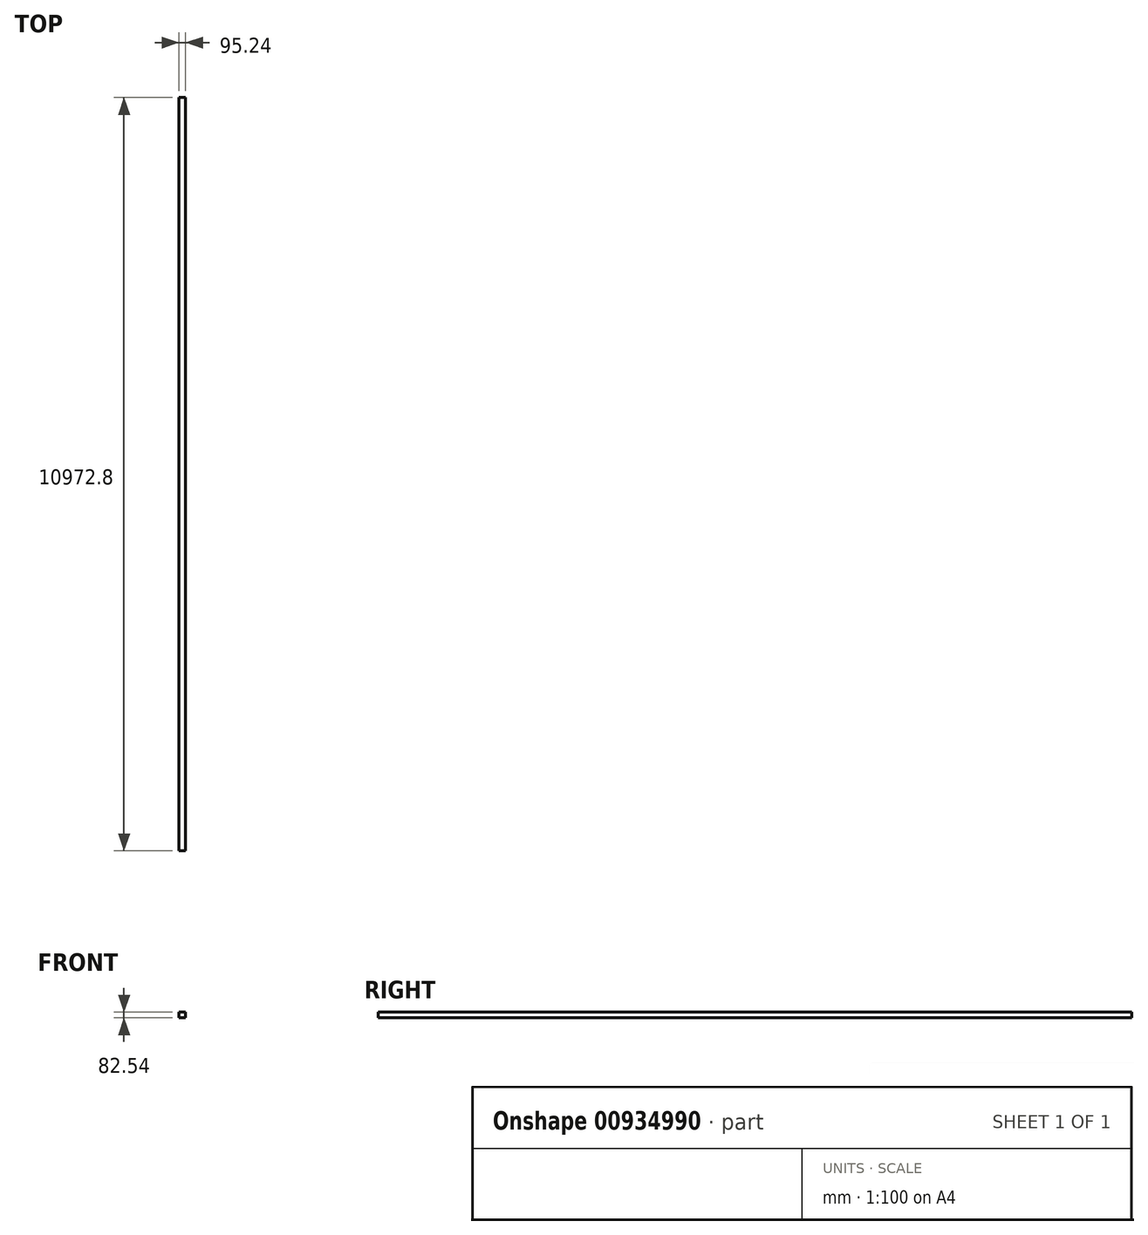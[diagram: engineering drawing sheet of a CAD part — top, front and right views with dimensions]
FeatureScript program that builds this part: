
annotation { "Feature Type Name" : "Feature", "Feature Type Description" : "" }
export const myFeature = defineFeature(function(context is Context, id is Id, definition is map)
    precondition{}
    {
        {
            var Q0;
            Q0=qCreatedBy(makeId("Front.planeOp"),FACE);
            var sketch = newSketch(context, id + "F0", { "sketchPlane" : qUnion([Q0])});
            skLineSegment(sketch, "E0.bottom", {"start": v(-47.62, 41.28) * mm, "end": v(47.63, 41.28) * mm});
            skLineSegment(sketch, "E0.top", {"start": v(-47.63, -41.28) * mm, "end": v(47.62, -41.28) * mm});
            skLineSegment(sketch, "E0.left", {"start": v(-47.62, 41.28) * mm, "end": v(-47.63, -41.28) * mm});
            skLineSegment(sketch, "E0.right", {"start": v(47.63, 41.28) * mm, "end": v(47.62, -41.28) * mm});
            skPoint(sketch, "E0.middle", {"position": v(0, 0) * mm});
            skSolve(sketch);
        }
        {
            var Q0;
            Q0=makeQuery(id+"F0.imprint","IMPRINT",FACE,{"disambiguationData":[TD([[makeQuery(id+"F0.imprint","IMPRINT",EDGE,{"derivedFrom":sQuery(id+"F0.wireOp",EDGE,"E0.bottom")}),-1.0]])]});
            extrude(context, id + "F1", {"entities" : qUnion([Q0]), "depth" : 10972.8 * mm, "offsetDistance" : 25.4 * mm});
        }
    });
